# Revit family: Door-Component_Button-Control_RPP
name_source: partatom
category: Generic Models
units: mm (PartAtom-declared; Revit-internal decimal feet)

## family parameters
Can host rebar = No
Classification Number = 23.30.40.11.34
Cut with Voids When Loaded = No
Host = Face
Maintain Annotation Orientation = No
Part Type = Normal
Room Calculation Point = No
Round Connector Dimension = Use Diameter
Shared = No

## types (1)
- Door-Component_Button-Control_RPP
    Assembly Code = F1030200
    Construction Details = http://www.arcat.com
    Default Elevation = 0' - 0"
    Description = Radiation Protection Products Product as Specified
    Expected Lifespan (Years) = 0
    Green Building-LEED = http://www.arcat.com
    Keynote = 13 49 00
    Maintenance Schedule (Months) = 0
    Manufacturer = Radiation Protection Products, Inc.
    Manufacturer Fax = 866-554-8445
    Manufacturer Website = http://www.radiationproducts.com
    Model = As Specified
    Product Data = http://www.arcat.com
    Product Properties = http://www.arcat.com
    Revision = R1_01_2014
    Sales Information = http://www.radiationproducts.com
    Send Message = http://www.arcat.com
    SpecWizard = http://www.arcat.com
    Specification = http://www.arcat.com
    Test Data = http://www.radiationproducts.com
    URL = http://www.radiationproducts.com
    Unit Depth = 0' - 0"
    Unit Height = 0' - 4 3/8"
    Unit Width = 0' - 7 15/16"
    Warranty Duration (Years) = 0

## geometry (parser evidence)
native form markers: Sweep x2
no freeform markers — native parametric forms only
